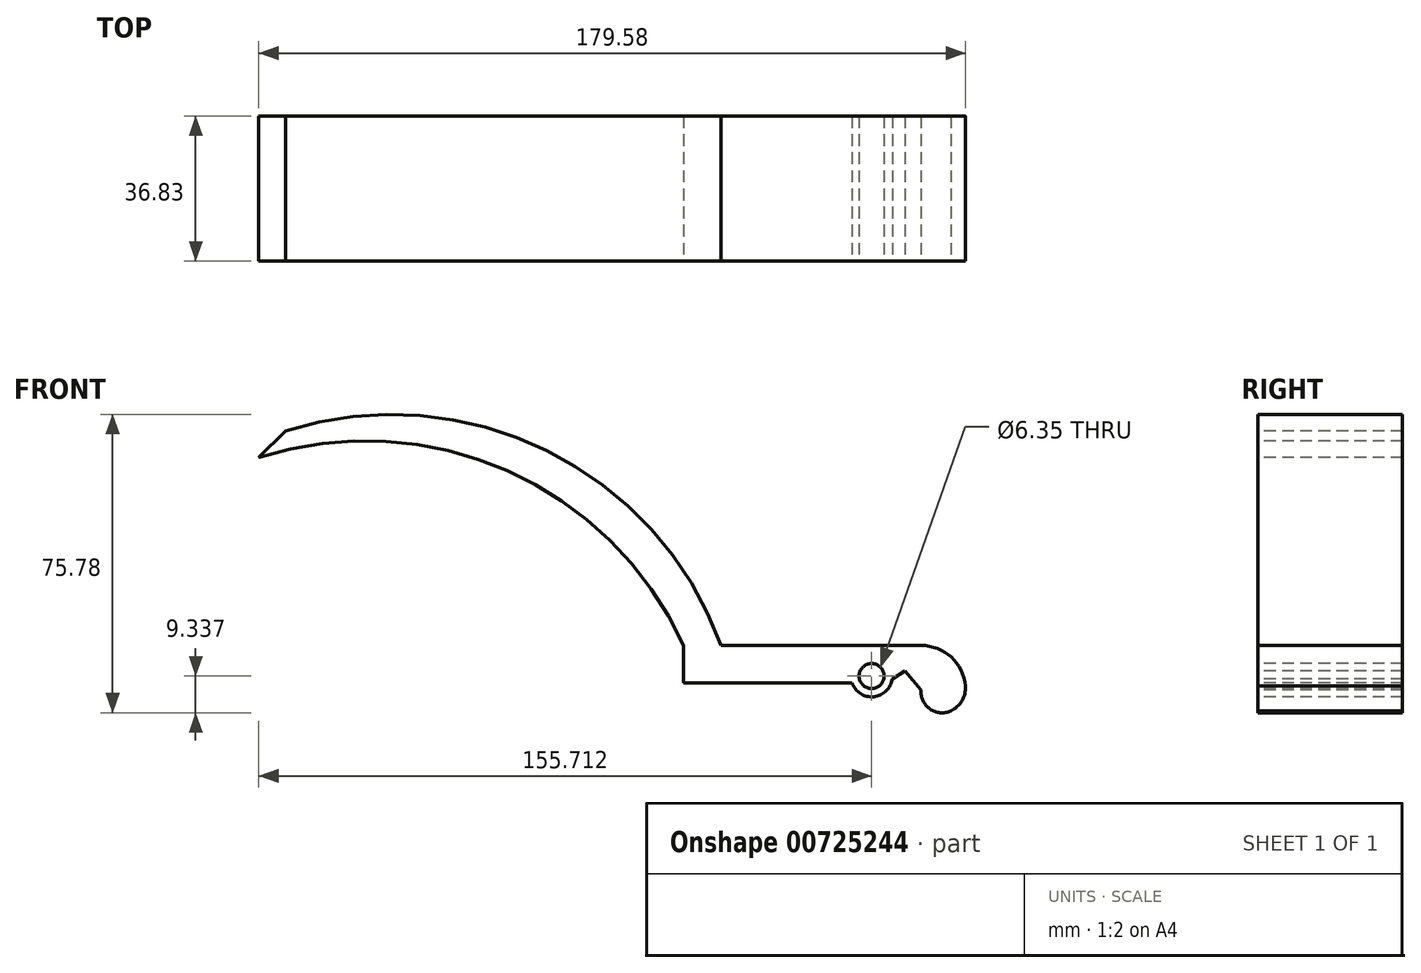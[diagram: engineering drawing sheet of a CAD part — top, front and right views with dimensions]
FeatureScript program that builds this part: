
annotation { "Feature Type Name" : "Feature", "Feature Type Description" : "" }
export const myFeature = defineFeature(function(context is Context, id is Id, definition is map)
    precondition{}
    {
        {
            var Q0;
            Q0=qCreatedBy(makeId("Front.planeOp"),FACE);
            var sketch = newSketch(context, id + "F0", { "sketchPlane" : qUnion([Q0])});
            skLineSegment(sketch, "E0", {"start": v(50.8, 0) * mm, "end": v(0, 0) * mm});
            skArc(sketch, "E1", {"start": v(0, 0) * mm, "mid": v(-44.36, 49.53) * mm, "end": v(-110.67, 54.43) * mm});
            skArc(sketch, "E2", {"start": v(62.09, -10.34) * mm, "mid": v(58.46, -2.98) * mm, "end": v(50.8, 0) * mm});
            skArc(sketch, "E3", {"start": v(58.35, -16.66) * mm, "mid": v(61.17, -14.06) * mm, "end": v(62.09, -10.34) * mm});
            skArc(sketch, "E4", {"start": v(50.8, -11.33) * mm, "mid": v(53.06, -16.14) * mm, "end": v(58.35, -16.66) * mm});
            skLineSegment(sketch, "E5", {"start": v(33.25, -9.52) * mm, "end": v(-9.52, -9.52) * mm});
            skLineSegment(sketch, "E6", {"start": v(-9.53, -9.53) * mm, "end": v(-9.53, 0) * mm});
            skArc(sketch, "E7", {"start": v(-9.53, 0) * mm, "mid": v(-54.43, 44.39) * mm, "end": v(-117.48, 47.77) * mm});
            skLineSegment(sketch, "E8", {"start": v(-117.48, 47.77) * mm, "end": v(-110.67, 54.43) * mm});
            skLineSegment(sketch, "E9", {"start": v(50.8, -11.33) * mm, "end": v(46.74, -6.5) * mm});
            skLineSegment(sketch, "E10", {"start": v(46.74, -6.5) * mm, "end": v(43.47, -8.45) * mm});
            skArc(sketch, "E11", {"start": v(33.25, -9.53) * mm, "mid": v(38.78, -13.03) * mm, "end": v(43.47, -8.45) * mm});
            skCircle(sketch, "E12", {"center": v(38.23, -7.78) * mm, "radius": 3.18 * mm});
            skSolve(sketch);
        }
        {
            var Q0;
            Q0=makeQuery(id+"F0.imprint","IMPRINT",FACE,{"disambiguationData":[TD([[makeQuery(id+"F0.imprint","IMPRINT",EDGE,{"derivedFrom":sQuery(id+"F0.wireOp",EDGE,"E0")}),1.0]])]});
            extrude(context, id + "F1", {"entities" : qUnion([Q0]), "oppositeDirection" : true, "depth" : 36.83 * mm, "offsetDistance" : 25.4 * mm});
        }
    });
